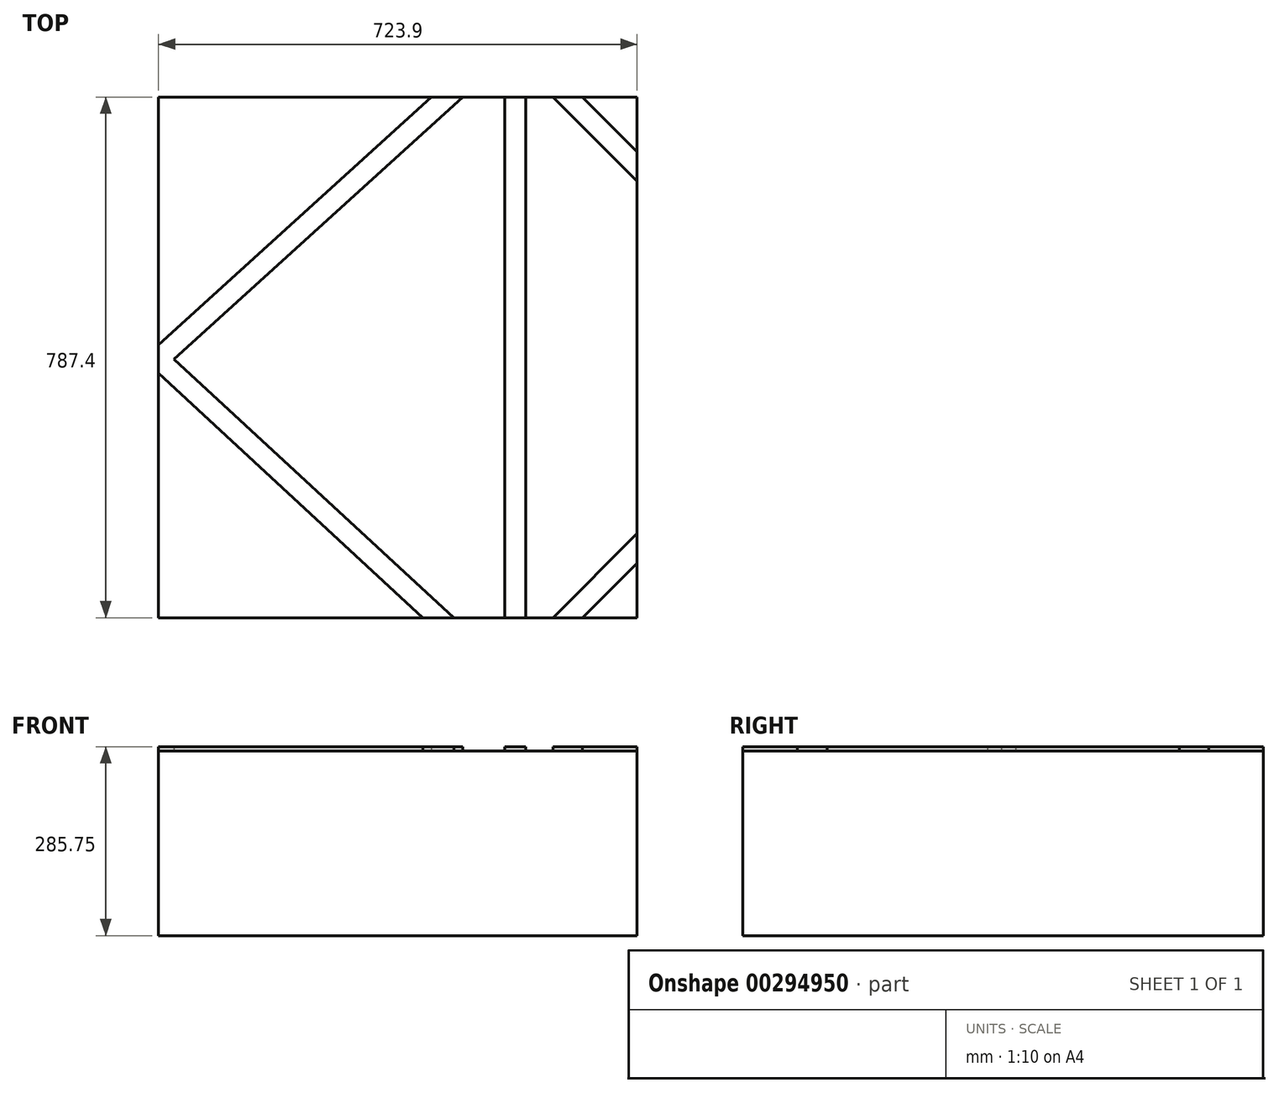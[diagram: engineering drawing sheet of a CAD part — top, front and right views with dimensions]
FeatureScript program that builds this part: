
annotation { "Feature Type Name" : "Feature", "Feature Type Description" : "" }
export const myFeature = defineFeature(function(context is Context, id is Id, definition is map)
    precondition{}
    {
        {
            var Q0;
            Q0=qCreatedBy(makeId("Top.planeOp"),FACE);
            var sketch = newSketch(context, id + "F0", { "sketchPlane" : qUnion([Q0])});
            skLineSegment(sketch, "E0.bottom", {"start": v(-361.95, 393.7) * mm, "end": v(361.95, 393.7) * mm});
            skLineSegment(sketch, "E0.top", {"start": v(-361.95, -393.7) * mm, "end": v(361.95, -393.7) * mm});
            skLineSegment(sketch, "E0.left", {"start": v(-361.95, 393.7) * mm, "end": v(-361.95, -393.7) * mm});
            skLineSegment(sketch, "E0.right", {"start": v(361.95, 393.7) * mm, "end": v(361.95, -393.7) * mm});
            skLineSegment(sketch, "E1", {"start": v(-361.95, 0) * mm, "end": v(361.95, 0) * mm, "construction": true});
            skLineSegment(sketch, "E2", {"start": v(0, 393.7) * mm, "end": v(0, -393.7) * mm, "construction": true});
            skSolve(sketch);
        }
        {
            var Q0;
            Q0 = qSketchRegion(id + "F0", true);
            extrude(context, id + "F1", {"entities" : qUnion([Q0]), "depth" : 279.4 * mm});
        }
        {
            var Q0;
            Q0=makeQuery(id+"F1.opExtrude","CAP_FACE",FACE,{"disambiguationData":[OSD([sQuery(id+"F0.wireOp",EDGE,"E0.bottom"),sQuery(id+"F0.wireOp",EDGE,"E0.top"),sQuery(id+"F0.wireOp",EDGE,"E0.left"),sQuery(id+"F0.wireOp",EDGE,"E0.right")])],"isStart":false});
            var sketch = newSketch(context, id + "F2", { "sketchPlane" : qUnion([Q0])});
            skLineSegment(sketch, "E3", {"start": v(-361.95, 19.05) * mm, "end": v(50.8, 393.7) * mm});
            skLineSegment(sketch, "E4", {"start": v(98.04, 393.7) * mm, "end": v(-361.95, -23.83) * mm});
            skPoint(sketch, "E5", {"position": v(-361.95, 0) * mm});
            skLineSegment(sketch, "E6", {"start": v(-361.95, -23.83) * mm, "end": v(38.1, -393.7) * mm});
            skLineSegment(sketch, "E7", {"start": v(84.48, -393.7) * mm, "end": v(-361.95, 19.05) * mm});
            skLineSegment(sketch, "E8", {"start": v(161.54, -393.7) * mm, "end": v(161.54, 393.7) * mm});
            skLineSegment(sketch, "E9", {"start": v(161.54, 393.7) * mm, "end": v(193.29, 393.7) * mm, "construction": true});
            skLineSegment(sketch, "E10", {"start": v(193.29, 393.7) * mm, "end": v(193.29, -393.7) * mm});
            skLineSegment(sketch, "E11", {"start": v(279.4, 393.7) * mm, "end": v(361.95, 311.15) * mm});
            skLineSegment(sketch, "E12", {"start": v(234.5, 393.7) * mm, "end": v(361.95, 266.25) * mm});
            skLineSegment(sketch, "E13", {"start": v(361.95, 0) * mm, "end": v(328.38, 0) * mm});
            skPoint(sketch, "E13.endSnap0", {"position": v(361.95, 0) * mm});
            skLineSegment(sketch, "E14.MirrorCS", {"start": v(234.5, -393.7) * mm, "end": v(361.95, -266.25) * mm});
            skLineSegment(sketch, "E15.MirrorCS", {"start": v(279.4, -393.7) * mm, "end": v(361.95, -311.15) * mm});
            skLineSegment(sketch, "E16", {"start": v(50.8, 393.7) * mm, "end": v(98.04, 393.7) * mm});
            skLineSegment(sketch, "E17", {"start": v(161.54, 393.7) * mm, "end": v(193.29, 393.7) * mm});
            skLineSegment(sketch, "E18", {"start": v(234.5, 393.7) * mm, "end": v(279.4, 393.7) * mm});
            skLineSegment(sketch, "E19", {"start": v(361.95, 311.15) * mm, "end": v(361.95, 266.25) * mm});
            skLineSegment(sketch, "E20", {"start": v(361.95, -266.25) * mm, "end": v(361.95, -311.15) * mm});
            skLineSegment(sketch, "E21", {"start": v(279.4, -393.7) * mm, "end": v(234.5, -393.7) * mm});
            skLineSegment(sketch, "E22", {"start": v(193.29, -393.7) * mm, "end": v(161.54, -393.7) * mm});
            skLineSegment(sketch, "E23", {"start": v(84.48, -393.7) * mm, "end": v(38.1, -393.7) * mm});
            skLineSegment(sketch, "E24", {"start": v(-361.95, -23.83) * mm, "end": v(-361.95, 19.05) * mm});
            skSolve(sketch);
        }
        {
            var Q0;
            Q0 = qSketchRegion(id + "F2", true);
            extrude(context, id + "F3", {"entities" : qUnion([Q0]), "depth" : 6.35 * mm});
        }
    });
